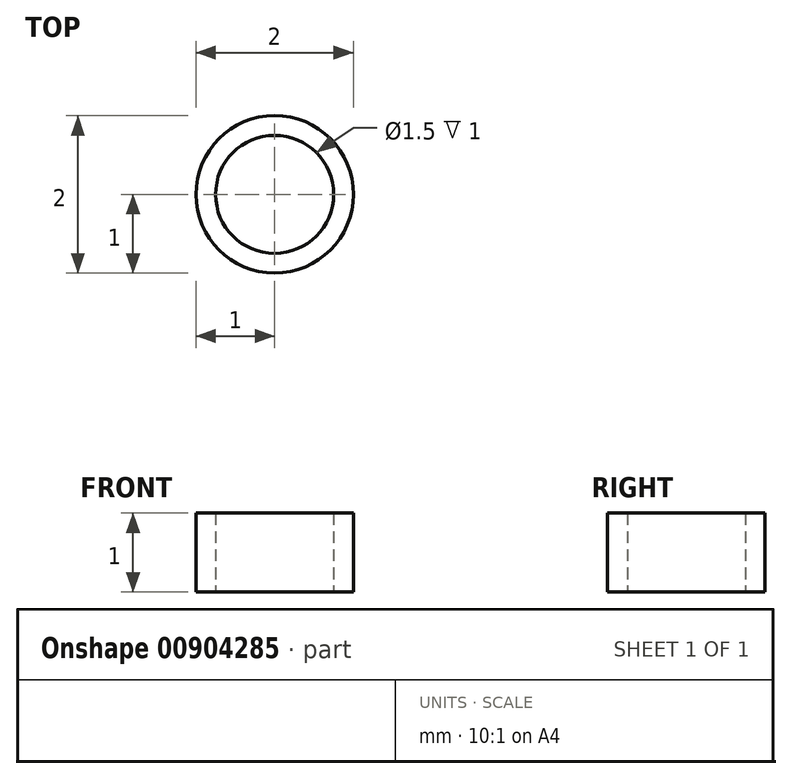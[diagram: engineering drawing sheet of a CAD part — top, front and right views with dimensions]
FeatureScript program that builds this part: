
annotation { "Feature Type Name" : "Feature", "Feature Type Description" : "" }
export const myFeature = defineFeature(function(context is Context, id is Id, definition is map)
    precondition{}
    {
        {
            var Q0;
            Q0=qCreatedBy(makeId("Front.planeOp"),FACE);
            var sketch = newSketch(context, id + "F0", { "sketchPlane" : qUnion([Q0])});
            skLineSegment(sketch, "E0.bottom", {"start": v(0, 0) * mm, "end": v(-0.75, 0) * mm});
            skLineSegment(sketch, "E0.top", {"start": v(0, 1) * mm, "end": v(-0.75, 1) * mm});
            skLineSegment(sketch, "E0.left", {"start": v(0, 0) * mm, "end": v(0, 1) * mm});
            skLineSegment(sketch, "E0.right", {"start": v(-0.75, 0) * mm, "end": v(-0.75, 1) * mm});
            skLineSegment(sketch, "E1.bottom", {"start": v(0, 0) * mm, "end": v(-1, 0) * mm});
            skLineSegment(sketch, "E1.top", {"start": v(0, 1) * mm, "end": v(-1, 1) * mm});
            skLineSegment(sketch, "E1.right", {"start": v(-1, 0) * mm, "end": v(-1, 1) * mm});
            skSolve(sketch);
        }
        {
            var Q0;
            {var subQ0=sQuery(id+"F0.wireOp",EDGE,"E0.right");Q0=makeQuery(id+"F0.imprint","IMPRINT",FACE,{"disambiguationData":[TD([[makeQuery(id+"F0.imprint","IMPRINT",EDGE,{"derivedFrom":subQ0}),1.0]])]});}
            var Q1;
            Q1=sQuery(id+"F0.wireOp",EDGE,"E0.left");
            revolve(context, id + "F1", {"surfaceOperationType" : NewSurfaceOperationType.NEW, "entities" : qUnion([Q0]), "axis" : qUnion([Q1]), "revolveType" : RevolveType.FULL});
        }
    });
